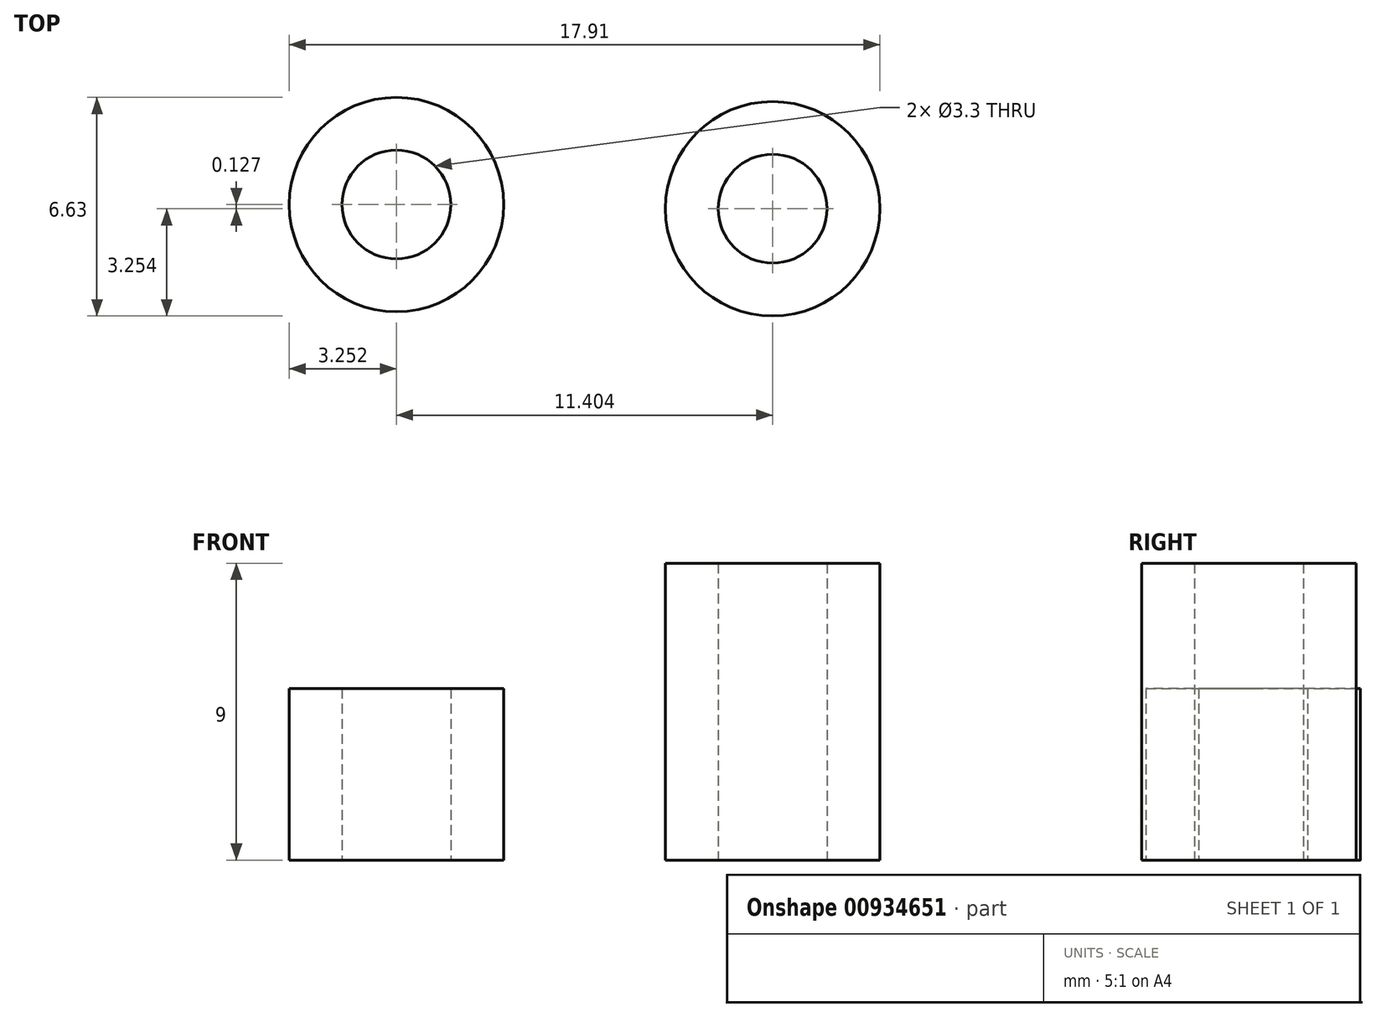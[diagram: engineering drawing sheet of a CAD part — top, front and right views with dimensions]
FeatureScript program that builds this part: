
annotation { "Feature Type Name" : "Feature", "Feature Type Description" : "" }
export const myFeature = defineFeature(function(context is Context, id is Id, definition is map)
    precondition{}
    {
        {
            assignVariable(context, id + "F0", {"name" : "len1", "anyValue" : 5.2});
        }
        {
            assignVariable(context, id + "F1", {"name" : "len2", "anyValue" : 9});
        }
        {
            var Q0;
            Q0=qCreatedBy(makeId("Top.planeOp"),FACE);
            var sketch = newSketch(context, id + "F2", { "sketchPlane" : qUnion([Q0])});
            skCircle(sketch, "E0", {"center": v(-4.02, 5.42) * mm, "radius": 1.65 * mm});
            skCircle(sketch, "E1.0", {"center": v(-4.02, 5.42) * mm, "radius": 3.25 * mm});
            skCircle(sketch, "E2", {"center": v(7.39, 5.3) * mm, "radius": 1.65 * mm});
            skCircle(sketch, "E3.0", {"center": v(7.39, 5.3) * mm, "radius": 3.25 * mm});
            skSolve(sketch);
        }
        {
            var Q0;
            Q0=makeQuery(id+"F2.imprint","IMPRINT",FACE,{"disambiguationData":[TD([[makeQuery(id+"F2.imprint","IMPRINT",EDGE,{"derivedFrom":sQuery(id+"F2.wireOp",EDGE,"E0")}),-1.0]])]});
            extrude(context, id + "F3", {"entities" : qUnion([Q0]), "depth" : (getVariable(context, 'len1')) * mm, "offsetDistance" : 25 * mm});
        }
        {
            var Q0;
            Q0=makeQuery(id+"F2.imprint","IMPRINT",FACE,{"disambiguationData":[TD([[makeQuery(id+"F2.imprint","IMPRINT",EDGE,{"derivedFrom":sQuery(id+"F2.wireOp",EDGE,"E2")}),-1.0]])]});
            extrude(context, id + "F4", {"entities" : qUnion([Q0]), "depth" : (getVariable(context, 'len2')) * mm, "offsetDistance" : 25 * mm});
        }
    });
